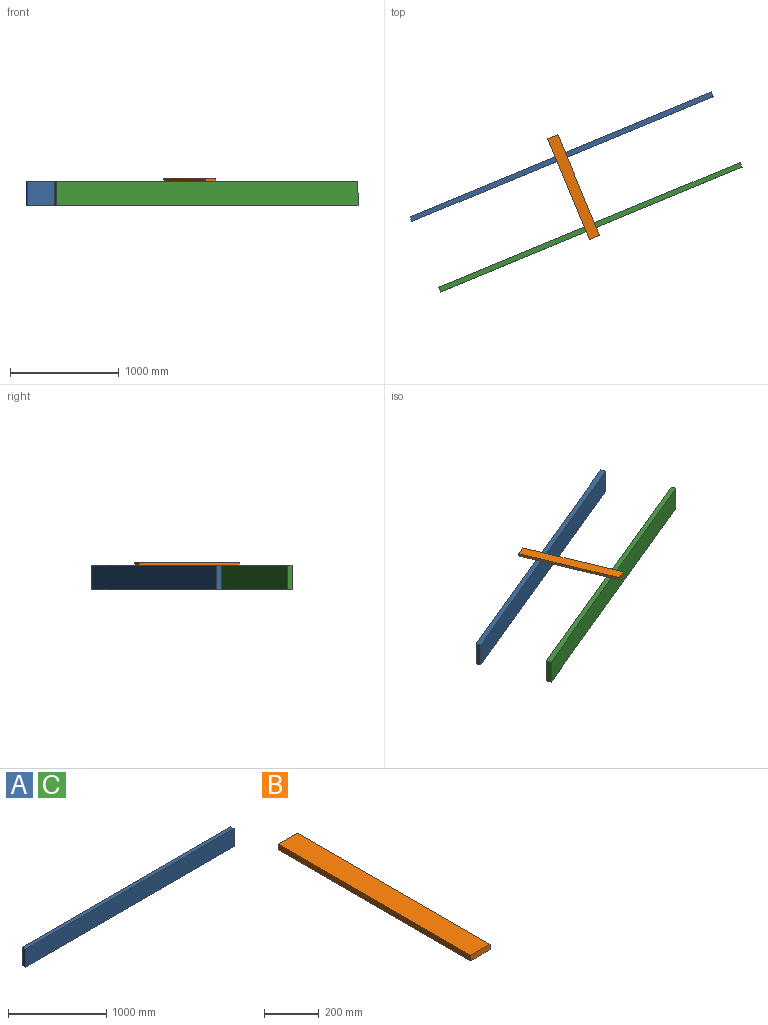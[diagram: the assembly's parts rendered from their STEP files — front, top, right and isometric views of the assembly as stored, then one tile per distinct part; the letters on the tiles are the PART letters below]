
ASSEMBLY  parts=3 mates=3
PART A: 6 faces, bbox 3000x47x225 mm
  f0: plane 3000x225mm, normal (0,-1,0), area 675000mm2, adj f1,f3,f4,f5
  f1: plane 3000x47mm, normal (0,0,-1), area 141000mm2, adj f0,f2,f4,f5
  f2: plane 3000x225mm, normal (0,1,0), area 675000mm2, adj f1,f3,f4,f5
  f3: plane 3000x47mm, normal (0,0,1), area 141000mm2, adj f0,f2,f4,f5
  f4: plane 225x47mm, normal (1,0,0), area 10575mm2, adj f0,f1,f2,f3
  f5: plane 225x47mm, normal (-1,0,0), area 10575mm2, adj f0,f1,f2,f3
PART B: 6 faces, bbox 100x1000x25 mm
  f0: plane 1000x25mm, normal (-1,0,0), area 25000mm2, adj f1,f3,f4,f5
  f1: plane 100x25mm, normal (0,-1,0), area 2500mm2, adj f0,f2,f4,f5
  f2: plane 1000x25mm, normal (1,0,0), area 25000mm2, adj f1,f3,f4,f5
  f3: plane 100x25mm, normal (0,1,0), area 2500mm2, adj f0,f2,f4,f5
  f4: plane 1000x100mm, normal (0,0,1), area 100000mm2, adj f0,f1,f2,f3
  f5: plane 1000x100mm, normal (0,0,-1), area 100000mm2, adj f0,f1,f2,f3
PART C: same geometry as A
PLACE A rot(axis=(-0.2,0.98,0),180deg) t=(2266.07,1165.25,184.38)mm
PLACE B rot(axis=(0,0,1),22.5deg) t=(1128.21,-148.97,184.38)mm
PLACE C rot(axis=(-0.2,0.98,0),180deg) t=(2530.68,515.42,184.38)mm
MATE fastened B.f5 <-> C.f1  axis (0,0,-1) through (1136.09,-37.45,184.38)mm
MATE planar C.f3 <-> A.f3  axis (0,0,-1) through (1136.09,-37.45,-40.62)mm
MATE parallel A.f0 <-> C.f2  axis (0.38,-0.92,0) through (880.47,590.68,71.88)mm
